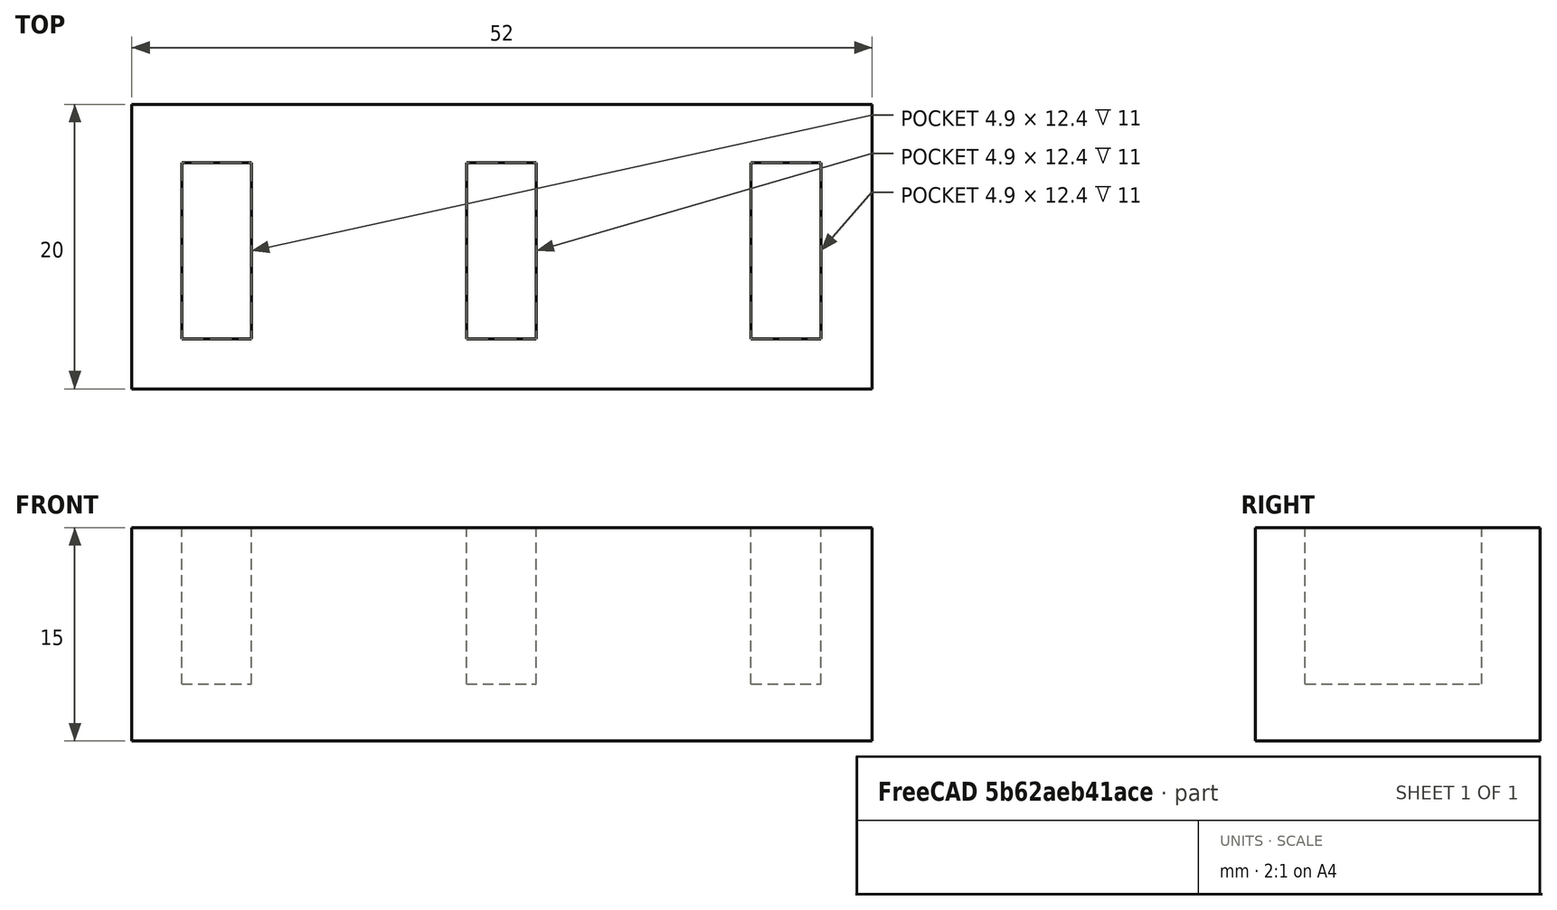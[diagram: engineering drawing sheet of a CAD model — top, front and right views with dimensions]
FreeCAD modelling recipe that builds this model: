
FCSTD DOCUMENT  (FreeCAD 0.17R13217 (Git))
Label: 06-porta-pendrive
License: All rights reserved
LicenseURL: http://en.wikipedia.org/wiki/All_rights_reserved
objects: Part::Box×4, Part::MultiFuse×1, Part::Cut×1
note: 6 computed .brp shape members not serialized (recipe doc carries the construction recipe); baked Part::Feature solids carry a one-line shape summary decoded from their .brp

FEATURE [Part::Box] Box  label="base"
  AttacherType = Attacher::AttachEngine3D
  Height = 15
  Length = 52
  Width = 20
FEATURE [Part::Box] Box001  label="slot1"
  AttacherType = Attacher::AttachEngine3D
  Height = 20
  Length = 4.9
  Placement = pos=(3.5,3.5,4) rot=(0,0,1;0rad)
  Width = 12.4
FEATURE [Part::Box] Box002  label="slot002"
  AttacherType = Attacher::AttachEngine3D
  Height = 20
  Length = 4.9
  Placement = pos=(23.5,3.5,4) rot=(0,0,1;0rad)
  Width = 12.4
FEATURE [Part::Box] Box003  label="slot003"
  AttacherType = Attacher::AttachEngine3D
  Height = 20
  Length = 4.9
  Placement = pos=(43.5,3.5,4) rot=(0,0,1;0rad)
  Width = 12.4
FEATURE [Part::MultiFuse] Fusion  label="slots"
  Refine = true
  Shapes = -> [Box001,Box003,Box002]
FEATURE [Part::Cut] Cut  label="objeto-final"
  Base = -> Box
  Refine = true
  Tool = -> Fusion
